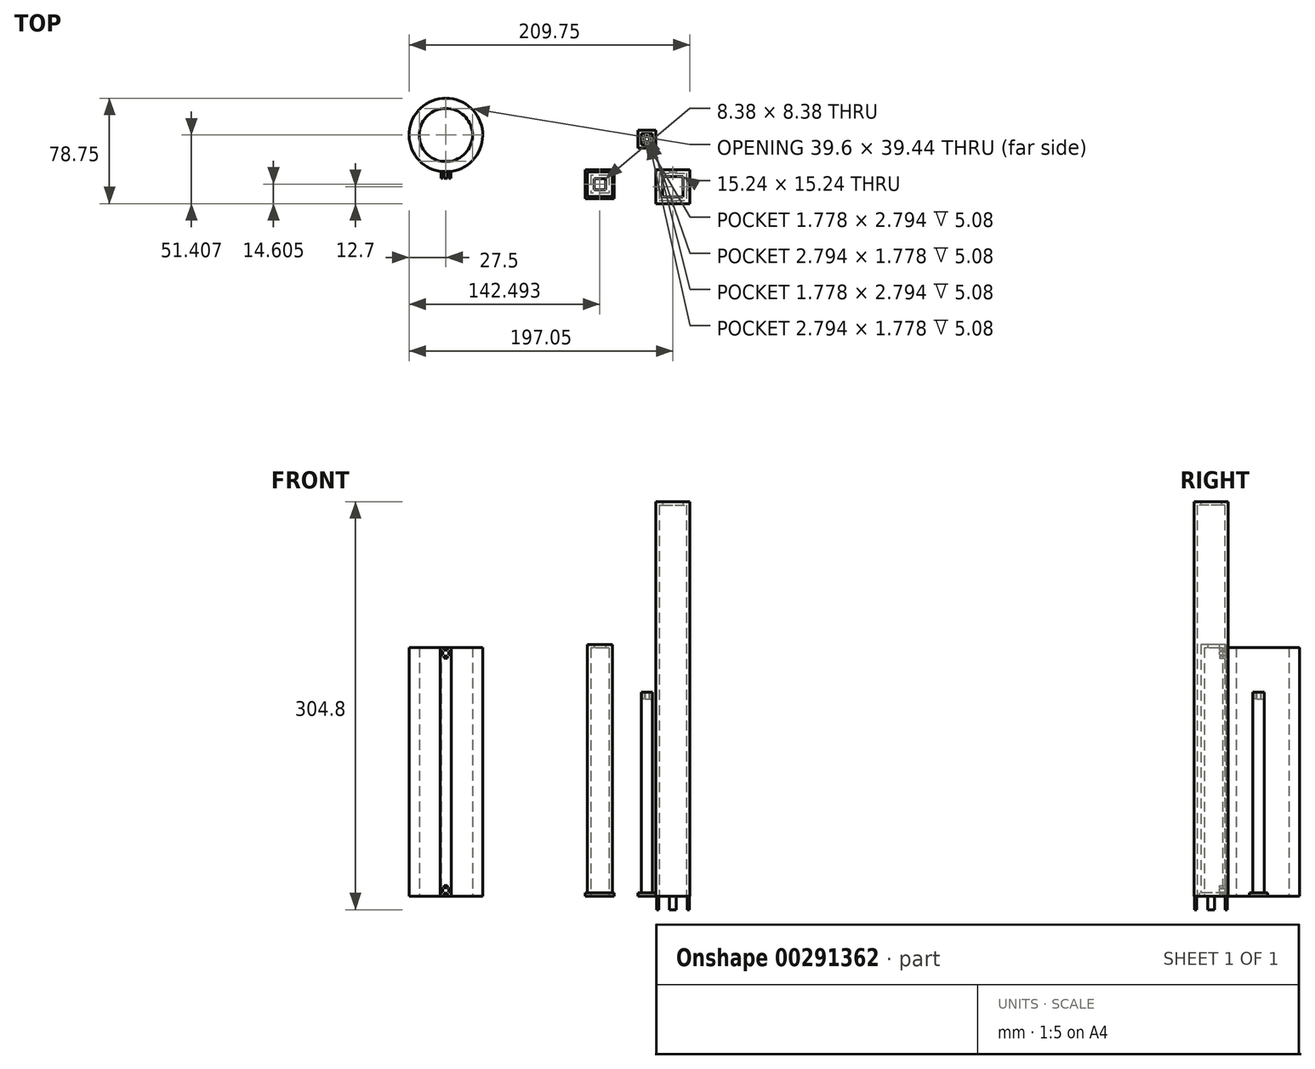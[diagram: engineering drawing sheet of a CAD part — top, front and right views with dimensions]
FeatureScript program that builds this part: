
annotation { "Feature Type Name" : "Feature", "Feature Type Description" : "" }
export const myFeature = defineFeature(function(context is Context, id is Id, definition is map)
    precondition{}
    {
        {
            var Q0;
            Q0=qCreatedBy(makeId("Top.planeOp"),FACE);
            var sketch = newSketch(context, id + "F0", { "sketchPlane" : qUnion([Q0])});
            skLineSegment(sketch, "E0.bottom", {"start": v(0, 0) * mm, "end": v(25.4, 0) * mm});
            skLineSegment(sketch, "E0.top", {"start": v(0, -25.4) * mm, "end": v(25.4, -25.4) * mm});
            skLineSegment(sketch, "E0.left", {"start": v(0, 0) * mm, "end": v(0, -25.4) * mm});
            skLineSegment(sketch, "E0.right", {"start": v(25.4, 0) * mm, "end": v(25.4, -25.4) * mm});
            skLineSegment(sketch, "E1.0", {"start": v(22.86, -2.54) * mm, "end": v(22.86, -22.86) * mm});
            skLineSegment(sketch, "E1.1", {"start": v(2.54, -2.54) * mm, "end": v(22.86, -2.54) * mm});
            skLineSegment(sketch, "E1.2", {"start": v(2.54, -2.54) * mm, "end": v(2.54, -22.86) * mm});
            skLineSegment(sketch, "E1.3", {"start": v(2.54, -22.86) * mm, "end": v(22.86, -22.86) * mm});
            skLineSegment(sketch, "E2.0", {"start": v(5.08, -5.08) * mm, "end": v(20.32, -5.08) * mm});
            skLineSegment(sketch, "E2.1", {"start": v(5.08, -5.08) * mm, "end": v(5.08, -20.32) * mm});
            skLineSegment(sketch, "E2.2", {"start": v(5.08, -20.32) * mm, "end": v(20.32, -20.32) * mm});
            skLineSegment(sketch, "E2.3", {"start": v(20.32, -5.08) * mm, "end": v(20.32, -20.32) * mm});
            skLineSegment(sketch, "E3.bottom", {"start": v(-31.06, 0) * mm, "end": v(-52.65, 0) * mm});
            skLineSegment(sketch, "E3.top", {"start": v(-31.06, -21.6) * mm, "end": v(-52.65, -21.6) * mm});
            skLineSegment(sketch, "E3.left", {"start": v(-31.06, 0) * mm, "end": v(-31.06, -21.6) * mm});
            skLineSegment(sketch, "E3.right", {"start": v(-52.65, 0) * mm, "end": v(-52.65, -21.6) * mm});
            skLineSegment(sketch, "E4.0", {"start": v(-32.59, -1.52) * mm, "end": v(-51.13, -1.52) * mm});
            skLineSegment(sketch, "E4.1", {"start": v(-32.59, -1.52) * mm, "end": v(-32.59, -20.07) * mm});
            skLineSegment(sketch, "E4.2", {"start": v(-32.59, -20.07) * mm, "end": v(-51.13, -20.07) * mm});
            skLineSegment(sketch, "E4.3", {"start": v(-51.13, -1.52) * mm, "end": v(-51.13, -20.07) * mm});
            skLineSegment(sketch, "E5.0", {"start": v(-35.13, -4.06) * mm, "end": v(-48.59, -4.06) * mm});
            skLineSegment(sketch, "E5.1", {"start": v(-35.13, -4.06) * mm, "end": v(-35.13, -17.53) * mm});
            skLineSegment(sketch, "E5.2", {"start": v(-35.13, -17.53) * mm, "end": v(-48.59, -17.53) * mm});
            skLineSegment(sketch, "E5.3", {"start": v(-48.59, -4.06) * mm, "end": v(-48.59, -17.53) * mm});
            skLineSegment(sketch, "E6.0", {"start": v(-37.67, -6.6) * mm, "end": v(-46.05, -6.6) * mm});
            skLineSegment(sketch, "E6.1", {"start": v(-37.67, -6.6) * mm, "end": v(-37.67, -14.99) * mm});
            skLineSegment(sketch, "E6.2", {"start": v(-37.67, -14.99) * mm, "end": v(-46.05, -14.99) * mm});
            skLineSegment(sketch, "E6.3", {"start": v(-46.05, -6.6) * mm, "end": v(-46.05, -14.99) * mm});
            skLineSegment(sketch, "E7.bottom", {"start": v(0, 29.56) * mm, "end": v(-13.46, 29.56) * mm});
            skLineSegment(sketch, "E7.top", {"start": v(0, 16.1) * mm, "end": v(-13.46, 16.1) * mm});
            skLineSegment(sketch, "E7.left", {"start": v(0, 29.56) * mm, "end": v(0, 16.1) * mm});
            skLineSegment(sketch, "E7.right", {"start": v(-13.46, 29.56) * mm, "end": v(-13.46, 16.1) * mm});
            skLineSegment(sketch, "E8.0", {"start": v(-2.54, 27.02) * mm, "end": v(-2.54, 18.64) * mm});
            skLineSegment(sketch, "E8.1", {"start": v(-2.54, 27.02) * mm, "end": v(-10.92, 27.02) * mm});
            skLineSegment(sketch, "E8.2", {"start": v(-10.92, 27.02) * mm, "end": v(-10.92, 18.64) * mm});
            skLineSegment(sketch, "E8.3", {"start": v(-2.54, 18.64) * mm, "end": v(-10.92, 18.64) * mm});
            skLineSegment(sketch, "E9.bottom", {"start": v(0.5, -15.24) * mm, "end": v(2.03, -15.24) * mm});
            skLineSegment(sketch, "E9.top", {"start": v(0.5, -10.16) * mm, "end": v(2.03, -10.16) * mm});
            skLineSegment(sketch, "E9.left", {"start": v(0.5, -15.24) * mm, "end": v(0.5, -10.16) * mm});
            skLineSegment(sketch, "E9.right", {"start": v(2.03, -15.24) * mm, "end": v(2.03, -10.16) * mm});
            skPoint(sketch, "E9.middle", {"position": v(1.27, -12.7) * mm});
            skLineSegment(sketch, "E10.bottom", {"start": v(23.37, -15.24) * mm, "end": v(24.9, -15.24) * mm});
            skLineSegment(sketch, "E10.top", {"start": v(23.37, -10.16) * mm, "end": v(24.9, -10.16) * mm});
            skLineSegment(sketch, "E10.left", {"start": v(23.37, -15.24) * mm, "end": v(23.37, -10.16) * mm});
            skLineSegment(sketch, "E10.right", {"start": v(24.9, -15.24) * mm, "end": v(24.9, -10.16) * mm});
            skPoint(sketch, "E10.middle", {"position": v(24.13, -12.7) * mm});
            skLineSegment(sketch, "E11.bottom", {"start": v(10.16, -0.5) * mm, "end": v(10.16, -2.03) * mm});
            skLineSegment(sketch, "E11.top", {"start": v(15.24, -0.5) * mm, "end": v(15.24, -2.03) * mm});
            skLineSegment(sketch, "E11.left", {"start": v(10.16, -0.5) * mm, "end": v(15.24, -0.5) * mm});
            skLineSegment(sketch, "E11.right", {"start": v(10.16, -2.03) * mm, "end": v(15.24, -2.03) * mm});
            skLineSegment(sketch, "E12", {"start": v(10.16, -1.27) * mm, "end": v(15.24, -1.27) * mm, "construction": true});
            skPoint(sketch, "E13", {"position": v(12.7, -1.27) * mm});
            skLineSegment(sketch, "E14.bottom", {"start": v(10.16, -23.37) * mm, "end": v(10.16, -24.9) * mm});
            skLineSegment(sketch, "E14.top", {"start": v(15.24, -23.37) * mm, "end": v(15.24, -24.9) * mm});
            skLineSegment(sketch, "E14.left", {"start": v(10.16, -23.37) * mm, "end": v(15.24, -23.37) * mm});
            skLineSegment(sketch, "E14.right", {"start": v(10.16, -24.9) * mm, "end": v(15.24, -24.9) * mm});
            skLineSegment(sketch, "E15", {"start": v(10.16, -24.13) * mm, "end": v(15.24, -24.13) * mm, "construction": true});
            skPoint(sketch, "E16", {"position": v(12.7, -24.13) * mm});
            skPoint(sketch, "E17.orphan", {"position": v(12.7, -2.03) * mm});
            skPoint(sketch, "E18.start.orphan", {"position": v(12.7, -0.5) * mm});
            skPoint(sketch, "E19.start.orphan", {"position": v(12.7, -2.54) * mm});
            skPoint(sketch, "E20.trimOffspring.end.orphan", {"position": v(12.7, 0) * mm});
            skPoint(sketch, "E21.trimOffspring.end.orphan", {"position": v(2.54, -12.7) * mm});
            skPoint(sketch, "E22.start.orphan", {"position": v(0, -12.7) * mm});
            skPoint(sketch, "E23.orphan", {"position": v(12.7, -25.4) * mm});
            skPoint(sketch, "E24.orphan", {"position": v(12.7, -22.86) * mm});
            skPoint(sketch, "E25.orphan", {"position": v(22.86, -12.7) * mm});
            skPoint(sketch, "E26.orphan", {"position": v(25.4, -12.7) * mm});
            skPoint(sketch, "E27.orphan", {"position": v(12.7, -23.37) * mm});
            skPoint(sketch, "E28.end.orphan", {"position": v(12.7, -24.9) * mm});
            skArc(sketch, "E29", {"start": v(-152.66, -1.33) * mm, "mid": v(-156.85, 53.35) * mm, "end": v(-161.04, -1.33) * mm});
            skLineSegment(sketch, "E30", {"start": v(-161.04, -1.33) * mm, "end": v(-152.66, -1.33) * mm});
            skArc(sketch, "E31.0", {"start": v(-153.3, 6.29) * mm, "mid": v(-156.85, 45.73) * mm, "end": v(-160.4, 6.29) * mm});
            skLineSegment(sketch, "E31.1", {"start": v(-160.4, 6.29) * mm, "end": v(-153.3, 6.29) * mm});
            skLineSegment(sketch, "E32.bottom", {"start": v(-10.92, 29.56) * mm, "end": v(-1.27, 29.56) * mm});
            skLineSegment(sketch, "E32.top", {"start": v(-10.92, 18.64) * mm, "end": v(-2.54, 18.64) * mm});
            skLineSegment(sketch, "E33", {"start": v(-10.92, 21.43) * mm, "end": v(-10.41, 21.43) * mm, "construction": true});
            skLineSegment(sketch, "E34", {"start": v(-10.41, 21.43) * mm, "end": v(-10.41, 24.23) * mm});
            skLineSegment(sketch, "E35", {"start": v(-10.41, 24.23) * mm, "end": v(-8.64, 24.23) * mm});
            skLineSegment(sketch, "E36", {"start": v(-8.64, 24.23) * mm, "end": v(-8.64, 21.43) * mm});
            skLineSegment(sketch, "E37", {"start": v(-8.64, 21.43) * mm, "end": v(-10.41, 21.43) * mm});
            skLineSegment(sketch, "E38", {"start": v(-10.41, 24.23) * mm, "end": v(-10.92, 24.23) * mm, "construction": true});
            skLineSegment(sketch, "E39", {"start": v(-8.13, 27.02) * mm, "end": v(-8.13, 26.51) * mm, "construction": true});
            skLineSegment(sketch, "E40", {"start": v(-8.13, 26.51) * mm, "end": v(-5.33, 26.51) * mm});
            skLineSegment(sketch, "E41", {"start": v(-5.33, 26.51) * mm, "end": v(-5.33, 24.73) * mm});
            skLineSegment(sketch, "E42", {"start": v(-5.33, 24.73) * mm, "end": v(-8.13, 24.73) * mm});
            skLineSegment(sketch, "E43", {"start": v(-8.13, 24.73) * mm, "end": v(-8.13, 26.51) * mm});
            skLineSegment(sketch, "E44", {"start": v(-5.33, 26.51) * mm, "end": v(-5.33, 27.02) * mm, "construction": true});
            skLineSegment(sketch, "E45", {"start": v(-2.54, 24.23) * mm, "end": v(-3.05, 24.23) * mm, "construction": true});
            skLineSegment(sketch, "E46", {"start": v(-3.05, 24.23) * mm, "end": v(-3.05, 21.43) * mm});
            skLineSegment(sketch, "E47", {"start": v(-3.05, 21.43) * mm, "end": v(-4.83, 21.43) * mm});
            skLineSegment(sketch, "E48", {"start": v(-4.83, 21.43) * mm, "end": v(-4.83, 24.23) * mm});
            skLineSegment(sketch, "E49", {"start": v(-4.83, 24.23) * mm, "end": v(-3.05, 24.23) * mm});
            skLineSegment(sketch, "E50", {"start": v(-3.05, 21.43) * mm, "end": v(-2.54, 21.43) * mm, "construction": true});
            skLineSegment(sketch, "E51", {"start": v(-5.33, 18.64) * mm, "end": v(-5.33, 19.15) * mm, "construction": true});
            skLineSegment(sketch, "E52", {"start": v(-5.33, 19.15) * mm, "end": v(-8.13, 19.15) * mm});
            skLineSegment(sketch, "E53", {"start": v(-8.13, 19.15) * mm, "end": v(-8.13, 20.92) * mm});
            skLineSegment(sketch, "E54", {"start": v(-8.13, 20.92) * mm, "end": v(-5.33, 20.92) * mm});
            skLineSegment(sketch, "E55", {"start": v(-5.33, 20.92) * mm, "end": v(-5.33, 19.15) * mm});
            skLineSegment(sketch, "E56", {"start": v(-8.13, 19.15) * mm, "end": v(-8.13, 18.64) * mm, "construction": true});
            skSolve(sketch);
        }
        {
            var Q0;
            Q0=makeQuery(id+"F0.imprint","IMPRINT",FACE,{"disambiguationData":[TD([[makeQuery(id+"F0.imprint","IMPRINT",EDGE,{"derivedFrom":sQuery(id+"F0.wireOp",EDGE,"E1.0")}),-1.0]])]});
            var Q1;
            Q1=makeQuery(id+"F0.imprint","IMPRINT",FACE,{"disambiguationData":[TD([[makeQuery(id+"F0.imprint","IMPRINT",EDGE,{"derivedFrom":sQuery(id+"F0.wireOp",EDGE,"E0.bottom")}),-1.0]])]});
            var Q2;
            Q2=makeQuery(id+"F0.imprint","IMPRINT",FACE,{"disambiguationData":[TD([[makeQuery(id+"F0.imprint","IMPRINT",EDGE,{"derivedFrom":sQuery(id+"F0.wireOp",EDGE,"E9.bottom")}),1.0]])]});
            var Q3;
            Q3=makeQuery(id+"F0.imprint","IMPRINT",FACE,{"disambiguationData":[TD([[makeQuery(id+"F0.imprint","IMPRINT",EDGE,{"derivedFrom":sQuery(id+"F0.wireOp",EDGE,"E14.bottom")}),1.0]])]});
            var Q4;
            Q4=makeQuery(id+"F0.imprint","IMPRINT",FACE,{"disambiguationData":[TD([[makeQuery(id+"F0.imprint","IMPRINT",EDGE,{"derivedFrom":sQuery(id+"F0.wireOp",EDGE,"E10.bottom")}),1.0]])]});
            var Q5;
            Q5=makeQuery(id+"F0.imprint","IMPRINT",FACE,{"disambiguationData":[TD([[makeQuery(id+"F0.imprint","IMPRINT",EDGE,{"derivedFrom":sQuery(id+"F0.wireOp",EDGE,"E11.bottom")}),1.0]])]});
            extrude(context, id + "F1", {"entities" : qUnion([Q0, Q1, Q2, Q3, Q4, Q5]), "depth" : 294.64 * mm});
        }
        {
            var Q0;
            Q0=makeQuery(id+"F0.imprint","IMPRINT",FACE,{"disambiguationData":[TD([[makeQuery(id+"F0.imprint","IMPRINT",EDGE,{"derivedFrom":sQuery(id+"F0.wireOp",EDGE,"E1.0")}),-1.0]])]});
            extrude(context, id + "F2", {"entities" : qUnion([Q0]), "operationType" : NewBodyOperationType.REMOVE, "depth" : 292.1 * mm});
        }
        {
            var Q0;
            Q0=makeQuery(id+"F0.imprint","IMPRINT",FACE,{"disambiguationData":[TD([[makeQuery(id+"F0.imprint","IMPRINT",EDGE,{"derivedFrom":sQuery(id+"F0.wireOp",EDGE,"E4.0")}),1.0]])]});
            var Q1;
            Q1=makeQuery(id+"F0.imprint","IMPRINT",FACE,{"disambiguationData":[TD([[makeQuery(id+"F0.imprint","IMPRINT",EDGE,{"derivedFrom":sQuery(id+"F0.wireOp",EDGE,"E5.0")}),1.0]])]});
            extrude(context, id + "F3", {"entities" : qUnion([Q0, Q1]), "depth" : 187.96 * mm});
        }
        {
            var Q0;
            Q0=makeQuery(id+"F0.imprint","IMPRINT",FACE,{"disambiguationData":[TD([[makeQuery(id+"F0.imprint","IMPRINT",EDGE,{"derivedFrom":sQuery(id+"F0.wireOp",EDGE,"E5.0")}),1.0]])]});
            extrude(context, id + "F4", {"entities" : qUnion([Q0]), "operationType" : NewBodyOperationType.REMOVE, "depth" : 185.42 * mm});
        }
        {
            var Q0;
            Q0=makeQuery(id+"F0.imprint","IMPRINT",FACE,{"disambiguationData":[TD([[makeQuery(id+"F0.imprint","IMPRINT",EDGE,{"derivedFrom":sQuery(id+"F0.wireOp",EDGE,"E3.bottom")}),1.0]])]});
            var Q1;
            Q1=makeQuery(id+"F0.imprint","IMPRINT",FACE,{"disambiguationData":[TD([[makeQuery(id+"F0.imprint","IMPRINT",EDGE,{"derivedFrom":sQuery(id+"F0.wireOp",EDGE,"E7.bottom")}),1.0]])]});
            extrude(context, id + "F5", {"entities" : qUnion([Q0, Q1]), "operationType" : NewBodyOperationType.ADD, "depth" : 2.54 * mm});
        }
        {
            var Q0;
            Q0=makeQuery(id+"F0.imprint","IMPRINT",FACE,{"disambiguationData":[TD([[makeQuery(id+"F0.imprint","IMPRINT",EDGE,{"derivedFrom":sQuery(id+"F0.wireOp",EDGE,"E9.bottom")}),1.0]])]});
            var Q1;
            Q1=makeQuery(id+"F0.imprint","IMPRINT",FACE,{"disambiguationData":[TD([[makeQuery(id+"F0.imprint","IMPRINT",EDGE,{"derivedFrom":sQuery(id+"F0.wireOp",EDGE,"E14.bottom")}),1.0]])]});
            var Q2;
            Q2=makeQuery(id+"F0.imprint","IMPRINT",FACE,{"disambiguationData":[TD([[makeQuery(id+"F0.imprint","IMPRINT",EDGE,{"derivedFrom":sQuery(id+"F0.wireOp",EDGE,"E11.bottom")}),1.0]])]});
            var Q3;
            Q3=makeQuery(id+"F0.imprint","IMPRINT",FACE,{"disambiguationData":[TD([[makeQuery(id+"F0.imprint","IMPRINT",EDGE,{"derivedFrom":sQuery(id+"F0.wireOp",EDGE,"E10.bottom")}),1.0]])]});
            extrude(context, id + "F6", {"entities" : qUnion([Q0, Q1, Q2, Q3]), "operationType" : NewBodyOperationType.ADD, "oppositeDirection" : true, "depth" : 10.16 * mm});
        }
        {
            var Q0;
            Q0=makeQuery(id+"F0.imprint","IMPRINT",FACE,{"disambiguationData":[TD([[makeQuery(id+"F0.imprint","IMPRINT",EDGE,{"derivedFrom":sQuery(id+"F0.wireOp",EDGE,"E29")}),1.0]])]});
            extrude(context, id + "F7", {"entities" : qUnion([Q0]), "depth" : 185.67 * mm});
        }
        {
            var Q0;
            Q0=makeQuery(id+"F7.opExtrude","SWEPT_FACE",FACE,{"disambiguationData":[OSD([sQuery(id+"F0.wireOp",EDGE,"E30")])]});
            var sketch = newSketch(context, id + "F8", { "sketchPlane" : qUnion([Q0])});
            skLineSegment(sketch, "E57.bottom", {"start": v(-161.04, 185.67) * mm, "end": v(-152.66, 185.67) * mm});
            skLineSegment(sketch, "E57.top", {"start": v(-161.04, 177.3) * mm, "end": v(-152.66, 177.3) * mm});
            skLineSegment(sketch, "E57.left", {"start": v(-161.04, 185.67) * mm, "end": v(-161.04, 177.3) * mm});
            skLineSegment(sketch, "E57.right", {"start": v(-152.66, 185.67) * mm, "end": v(-152.66, 177.3) * mm});
            skLineSegment(sketch, "E58", {"start": v(-161.04, 180.21) * mm, "end": v(-160.53, 180.21) * mm, "construction": true});
            skLineSegment(sketch, "E59", {"start": v(-160.53, 180.21) * mm, "end": v(-160.53, 182.75) * mm});
            skLineSegment(sketch, "E60", {"start": v(-160.53, 182.75) * mm, "end": v(-159, 182.75) * mm});
            skLineSegment(sketch, "E61", {"start": v(-159, 182.75) * mm, "end": v(-159, 180.21) * mm});
            skLineSegment(sketch, "E62", {"start": v(-159, 180.21) * mm, "end": v(-160.53, 180.21) * mm});
            skLineSegment(sketch, "E63", {"start": v(-160.53, 182.75) * mm, "end": v(-161.04, 182.75) * mm, "construction": true});
            skLineSegment(sketch, "E64", {"start": v(-158.12, 185.67) * mm, "end": v(-158.12, 185.17) * mm, "construction": true});
            skLineSegment(sketch, "E65", {"start": v(-158.12, 185.17) * mm, "end": v(-155.58, 185.17) * mm});
            skLineSegment(sketch, "E66", {"start": v(-155.58, 185.17) * mm, "end": v(-155.58, 183.64) * mm});
            skLineSegment(sketch, "E67", {"start": v(-155.58, 183.64) * mm, "end": v(-158.12, 183.64) * mm});
            skLineSegment(sketch, "E68", {"start": v(-158.12, 183.64) * mm, "end": v(-158.12, 185.17) * mm});
            skLineSegment(sketch, "E69", {"start": v(-155.58, 185.17) * mm, "end": v(-155.58, 185.67) * mm, "construction": true});
            skLineSegment(sketch, "E70", {"start": v(-152.66, 182.75) * mm, "end": v(-153.17, 182.75) * mm, "construction": true});
            skLineSegment(sketch, "E71", {"start": v(-153.17, 182.75) * mm, "end": v(-153.17, 180.21) * mm});
            skLineSegment(sketch, "E72", {"start": v(-153.17, 180.21) * mm, "end": v(-154.7, 180.21) * mm});
            skLineSegment(sketch, "E73", {"start": v(-154.7, 180.21) * mm, "end": v(-154.7, 182.75) * mm});
            skLineSegment(sketch, "E74", {"start": v(-154.7, 182.75) * mm, "end": v(-153.17, 182.75) * mm});
            skLineSegment(sketch, "E75", {"start": v(-153.17, 180.21) * mm, "end": v(-152.66, 180.21) * mm, "construction": true});
            skLineSegment(sketch, "E76", {"start": v(-155.58, 177.3) * mm, "end": v(-155.58, 177.8) * mm, "construction": true});
            skLineSegment(sketch, "E77", {"start": v(-155.58, 177.8) * mm, "end": v(-158.12, 177.8) * mm});
            skLineSegment(sketch, "E78", {"start": v(-158.12, 177.8) * mm, "end": v(-158.12, 179.32) * mm});
            skLineSegment(sketch, "E79", {"start": v(-158.12, 179.32) * mm, "end": v(-155.58, 179.32) * mm});
            skLineSegment(sketch, "E80", {"start": v(-155.58, 179.32) * mm, "end": v(-155.58, 177.8) * mm});
            skLineSegment(sketch, "E81", {"start": v(-158.12, 177.8) * mm, "end": v(-158.12, 177.3) * mm, "construction": true});
            skLineSegment(sketch, "E82.bottom", {"start": v(-161.04, 8.38) * mm, "end": v(-152.66, 8.38) * mm});
            skLineSegment(sketch, "E82.top", {"start": v(-161.04, 0) * mm, "end": v(-152.66, 0) * mm});
            skLineSegment(sketch, "E82.left", {"start": v(-161.04, 8.38) * mm, "end": v(-161.04, 0) * mm});
            skLineSegment(sketch, "E82.right", {"start": v(-152.66, 8.38) * mm, "end": v(-152.66, 0) * mm});
            skLineSegment(sketch, "E83", {"start": v(-161.04, 2.92) * mm, "end": v(-160.53, 2.92) * mm, "construction": true});
            skLineSegment(sketch, "E84", {"start": v(-160.53, 2.92) * mm, "end": v(-160.53, 5.46) * mm});
            skLineSegment(sketch, "E85", {"start": v(-160.53, 5.46) * mm, "end": v(-159, 5.46) * mm});
            skLineSegment(sketch, "E86", {"start": v(-159, 5.46) * mm, "end": v(-159, 2.92) * mm});
            skLineSegment(sketch, "E87", {"start": v(-159, 2.92) * mm, "end": v(-160.53, 2.92) * mm});
            skLineSegment(sketch, "E88", {"start": v(-160.53, 5.46) * mm, "end": v(-161.04, 5.46) * mm, "construction": true});
            skLineSegment(sketch, "E89", {"start": v(-158.12, 8.38) * mm, "end": v(-158.12, 7.87) * mm, "construction": true});
            skLineSegment(sketch, "E90", {"start": v(-158.12, 7.87) * mm, "end": v(-155.58, 7.87) * mm});
            skLineSegment(sketch, "E91", {"start": v(-155.58, 7.87) * mm, "end": v(-155.58, 6.35) * mm});
            skLineSegment(sketch, "E92", {"start": v(-155.58, 6.35) * mm, "end": v(-158.12, 6.35) * mm});
            skLineSegment(sketch, "E93", {"start": v(-158.12, 6.35) * mm, "end": v(-158.12, 7.87) * mm});
            skLineSegment(sketch, "E94", {"start": v(-155.58, 7.87) * mm, "end": v(-155.58, 8.38) * mm, "construction": true});
            skLineSegment(sketch, "E95", {"start": v(-152.66, 5.46) * mm, "end": v(-153.17, 5.46) * mm, "construction": true});
            skLineSegment(sketch, "E96", {"start": v(-153.17, 5.46) * mm, "end": v(-153.17, 2.92) * mm});
            skLineSegment(sketch, "E97", {"start": v(-153.17, 2.92) * mm, "end": v(-154.7, 2.92) * mm});
            skLineSegment(sketch, "E98", {"start": v(-154.7, 2.92) * mm, "end": v(-154.7, 5.46) * mm});
            skLineSegment(sketch, "E99", {"start": v(-154.7, 5.46) * mm, "end": v(-153.17, 5.46) * mm});
            skLineSegment(sketch, "E100", {"start": v(-153.17, 2.92) * mm, "end": v(-152.66, 2.92) * mm, "construction": true});
            skLineSegment(sketch, "E101", {"start": v(-155.58, 0) * mm, "end": v(-155.58, 0.5) * mm, "construction": true});
            skLineSegment(sketch, "E102", {"start": v(-155.58, 0.5) * mm, "end": v(-158.12, 0.5) * mm});
            skLineSegment(sketch, "E103", {"start": v(-158.12, 0.5) * mm, "end": v(-158.12, 2.03) * mm});
            skLineSegment(sketch, "E104", {"start": v(-158.12, 2.03) * mm, "end": v(-155.58, 2.03) * mm});
            skLineSegment(sketch, "E105", {"start": v(-155.58, 2.03) * mm, "end": v(-155.58, 0.5) * mm});
            skLineSegment(sketch, "E106", {"start": v(-158.12, 0.5) * mm, "end": v(-158.12, 0) * mm, "construction": true});
            skSolve(sketch);
        }
        {
            var Q0;
            Q0=makeQuery(id+"F8.imprint","IMPRINT",FACE,{"disambiguationData":[TD([[makeQuery(id+"F8.imprint","IMPRINT",EDGE,{"derivedFrom":sQuery(id+"F8.wireOp",EDGE,"E59")}),-1.0]])]});
            var Q1;
            Q1=makeQuery(id+"F8.imprint","IMPRINT",FACE,{"disambiguationData":[TD([[makeQuery(id+"F8.imprint","IMPRINT",EDGE,{"derivedFrom":sQuery(id+"F8.wireOp",EDGE,"E65")}),-1.0]])]});
            var Q2;
            Q2=makeQuery(id+"F8.imprint","IMPRINT",FACE,{"disambiguationData":[TD([[makeQuery(id+"F8.imprint","IMPRINT",EDGE,{"derivedFrom":sQuery(id+"F8.wireOp",EDGE,"E71")}),-1.0]])]});
            var Q3;
            Q3=makeQuery(id+"F8.imprint","IMPRINT",FACE,{"disambiguationData":[TD([[makeQuery(id+"F8.imprint","IMPRINT",EDGE,{"derivedFrom":sQuery(id+"F8.wireOp",EDGE,"E77")}),-1.0]])]});
            var Q4;
            Q4=makeQuery(id+"F8.imprint","IMPRINT",FACE,{"disambiguationData":[TD([[makeQuery(id+"F8.imprint","IMPRINT",EDGE,{"derivedFrom":sQuery(id+"F8.wireOp",EDGE,"E84")}),-1.0]])]});
            var Q5;
            Q5=makeQuery(id+"F8.imprint","IMPRINT",FACE,{"disambiguationData":[TD([[makeQuery(id+"F8.imprint","IMPRINT",EDGE,{"derivedFrom":sQuery(id+"F8.wireOp",EDGE,"E90")}),-1.0]])]});
            var Q6;
            Q6=makeQuery(id+"F8.imprint","IMPRINT",FACE,{"disambiguationData":[TD([[makeQuery(id+"F8.imprint","IMPRINT",EDGE,{"derivedFrom":sQuery(id+"F8.wireOp",EDGE,"E96")}),-1.0]])]});
            var Q7;
            Q7=makeQuery(id+"F8.imprint","IMPRINT",FACE,{"disambiguationData":[TD([[makeQuery(id+"F8.imprint","IMPRINT",EDGE,{"derivedFrom":sQuery(id+"F8.wireOp",EDGE,"E102")}),-1.0]])]});
            extrude(context, id + "F9", {"entities" : qUnion([Q0, Q1, Q2, Q3, Q4, Q5, Q6, Q7]), "operationType" : NewBodyOperationType.ADD, "depth" : 4.95 * mm});
        }
        {
            var Q0;
            Q0=makeQuery(id+"F0.imprint","IMPRINT",FACE,{"disambiguationData":[TD([[makeQuery(id+"F0.imprint","IMPRINT",EDGE,{"derivedFrom":sQuery(id+"F0.wireOp",EDGE,"E8.0")}),-1.0]])]});
            extrude(context, id + "F10", {"entities" : qUnion([Q0]), "operationType" : NewBodyOperationType.ADD, "depth" : 152.4 * mm});
        }
        {
            var Q0;
            Q0=makeQuery(id+"F0.imprint","IMPRINT",FACE,{"disambiguationData":[TD([[makeQuery(id+"F0.imprint","IMPRINT",EDGE,{"derivedFrom":sQuery(id+"F0.wireOp",EDGE,"E52")}),-1.0]])]});
            var Q1;
            Q1=makeQuery(id+"F0.imprint","IMPRINT",FACE,{"disambiguationData":[TD([[makeQuery(id+"F0.imprint","IMPRINT",EDGE,{"derivedFrom":sQuery(id+"F0.wireOp",EDGE,"E34")}),-1.0]])]});
            var Q2;
            Q2=makeQuery(id+"F0.imprint","IMPRINT",FACE,{"disambiguationData":[TD([[makeQuery(id+"F0.imprint","IMPRINT",EDGE,{"derivedFrom":sQuery(id+"F0.wireOp",EDGE,"E40")}),-1.0]])]});
            var Q3;
            Q3=makeQuery(id+"F0.imprint","IMPRINT",FACE,{"disambiguationData":[TD([[makeQuery(id+"F0.imprint","IMPRINT",EDGE,{"derivedFrom":sQuery(id+"F0.wireOp",EDGE,"E46")}),-1.0]])]});
            extrude(context, id + "F11", {"entities" : qUnion([Q0, Q1, Q2, Q3]), "operationType" : NewBodyOperationType.ADD, "depth" : 147.32 * mm});
        }
    });
